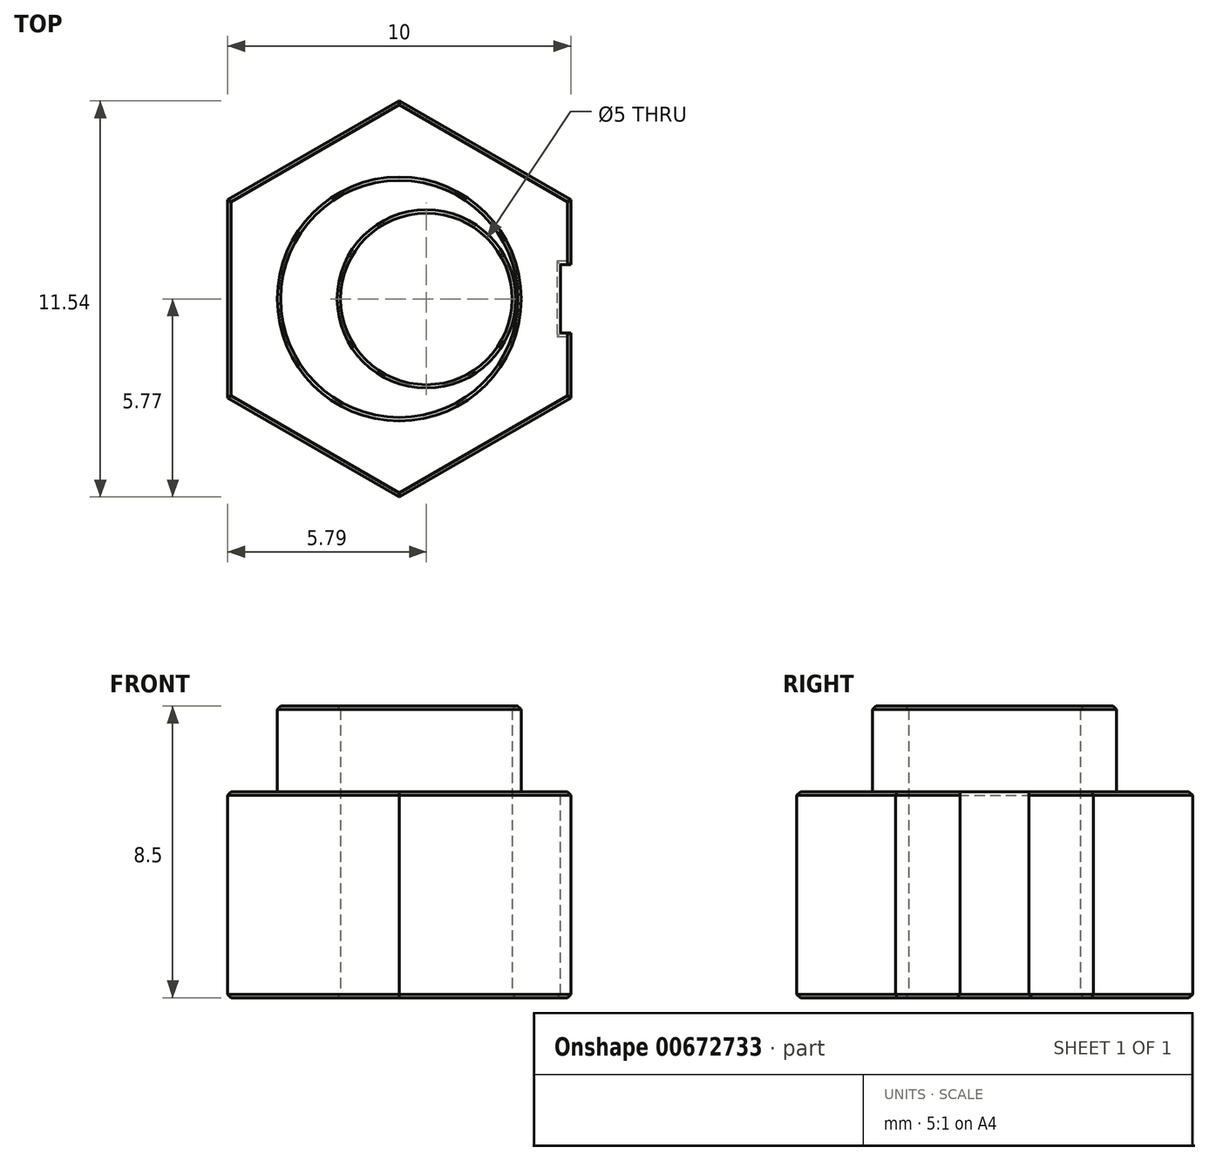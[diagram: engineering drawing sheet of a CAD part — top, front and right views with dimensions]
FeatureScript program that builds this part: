
annotation { "Feature Type Name" : "Feature", "Feature Type Description" : "" }
export const myFeature = defineFeature(function(context is Context, id is Id, definition is map)
    precondition{}
    {
        {
            var Q0;
            Q0=qCreatedBy(makeId("Top.planeOp"),FACE);
            var sketch = newSketch(context, id + "F0", { "sketchPlane" : qUnion([Q0])});
            skCircle(sketch, "E0.cCircle", {"center": v(0, 0) * mm, "radius": 5 * mm, "construction": true});
            skLineSegment(sketch, "E0.0", {"start": v(5, 2.89) * mm, "end": v(5, -2.89) * mm});
            skLineSegment(sketch, "E0.1", {"start": v(5, -2.89) * mm, "end": v(0, -5.77) * mm});
            skLineSegment(sketch, "E0.2", {"start": v(0, -5.77) * mm, "end": v(-5, -2.89) * mm});
            skLineSegment(sketch, "E0.3", {"start": v(-5, -2.89) * mm, "end": v(-5, 2.89) * mm});
            skLineSegment(sketch, "E0.4", {"start": v(-5, 2.89) * mm, "end": v(0, 5.77) * mm});
            skLineSegment(sketch, "E0.5", {"start": v(0, 5.77) * mm, "end": v(5, 2.89) * mm});
            skPoint(sketch, "E0.0.midPoint", {"position": v(5, 0) * mm});
            skSolve(sketch);
        }
        {
            var Q0;
            Q0=makeQuery(id+"F0.imprint","IMPRINT",FACE,{"disambiguationData":[TD([[makeQuery(id+"F0.imprint","IMPRINT",EDGE,{"derivedFrom":sQuery(id+"F0.wireOp",EDGE,"E0.0")}),-1.0]])]});
            extrude(context, id + "F1", {"entities" : qUnion([Q0]), "depth" : 6 * mm, "offsetDistance" : 25 * mm});
        }
        {
            var Q0;
            Q0=makeQuery(id+"F1.opExtrude","CAP_FACE",FACE,{"disambiguationData":[OSD([sQuery(id+"F0.wireOp",EDGE,"E0.0"),sQuery(id+"F0.wireOp",EDGE,"E0.1"),sQuery(id+"F0.wireOp",EDGE,"E0.2"),sQuery(id+"F0.wireOp",EDGE,"E0.3"),sQuery(id+"F0.wireOp",EDGE,"E0.4"),sQuery(id+"F0.wireOp",EDGE,"E0.5")])],"isStart":false});
            var sketch = newSketch(context, id + "F2", { "sketchPlane" : qUnion([Q0])});
            skCircle(sketch, "E1", {"center": v(0, 0) * mm, "radius": 3.56 * mm});
            skCircle(sketch, "E2", {"center": v(0.79, 0) * mm, "radius": 2.5 * mm});
            skSolve(sketch);
        }
        {
            var Q0;
            Q0=makeQuery(id+"F2.imprint","IMPRINT",FACE,{"disambiguationData":[TD([[makeQuery(id+"F2.imprint","IMPRINT",EDGE,{"derivedFrom":sQuery(id+"F2.wireOp",EDGE,"E1")}),1.0]])]});
            extrude(context, id + "F3", {"entities" : qUnion([Q0]), "operationType" : NewBodyOperationType.ADD, "depth" : 2.5 * mm, "offsetDistance" : 25 * mm});
        }
        {
            var Q0;
            {var subQ0=sQuery(id+"F0.wireOp",EDGE,"E0.2");var subQ1=sQuery(id+"F0.wireOp",EDGE,"E0.1");var subQ2=sQuery(id+"F0.wireOp",EDGE,"E0.3");var subQ3=sQuery(id+"F0.wireOp",EDGE,"E0.0");var subQ4=sQuery(id+"F0.wireOp",EDGE,"E0.4");var subQ5=sQuery(id+"F0.wireOp",EDGE,"E0.5");Q0=makeQuery(id+"F3.boolean.opBoolean","SPLIT",FACE,{"disambiguationData":[TD([makeQuery(id+"F1.opExtrude","SWEPT_FACE",FACE,{"disambiguationData":[OSD([subQ3])]})])],"derivedFrom":makeQuery(id+"F1.opExtrude","CAP_FACE",FACE,{"disambiguationData":[OSD([subQ3,subQ1,subQ0,subQ2,subQ4,subQ5])],"isStart":false})});}
            var sketch = newSketch(context, id + "F4", { "sketchPlane" : qUnion([Q0])});
            skLineSegment(sketch, "E3.bottom", {"start": v(5, 1) * mm, "end": v(4.7, 1) * mm});
            skLineSegment(sketch, "E3.top", {"start": v(5, -1) * mm, "end": v(4.7, -1) * mm});
            skLineSegment(sketch, "E3.left", {"start": v(5, 1) * mm, "end": v(5, -1) * mm});
            skLineSegment(sketch, "E3.right", {"start": v(4.7, 1) * mm, "end": v(4.7, -1) * mm});
            skLineSegment(sketch, "E4", {"start": v(0, 0) * mm, "end": v(5, 0) * mm, "construction": true});
            skSolve(sketch);
        }
        {
            var Q0;
            Q0=makeQuery(id+"F4.imprint","IMPRINT",FACE,{"disambiguationData":[TD([[makeQuery(id+"F4.imprint","IMPRINT",EDGE,{"derivedFrom":sQuery(id+"F4.wireOp",EDGE,"E3.bottom")}),1.0]])]});
            extrude(context, id + "F5", {"entities" : qUnion([Q0]), "operationType" : NewBodyOperationType.REMOVE, "oppositeDirection" : true, "depth" : 25 * mm, "offsetDistance" : 25 * mm});
        }
        {
            var Q0;
            Q0=makeQuery(id+"F3.boolean.opBoolean","SPLIT",FACE,{"disambiguationData":[TD([makeQuery(id+"F3.opExtrude","SWEPT_FACE",FACE,{"disambiguationData":[OSD([sQuery(id+"F2.wireOp",EDGE,"E2")])]})])],"derivedFrom":makeQuery(id+"F1.opExtrude","CAP_FACE",FACE,{"disambiguationData":[OSD([sQuery(id+"F0.wireOp",EDGE,"E0.0"),sQuery(id+"F0.wireOp",EDGE,"E0.1"),sQuery(id+"F0.wireOp",EDGE,"E0.2"),sQuery(id+"F0.wireOp",EDGE,"E0.3"),sQuery(id+"F0.wireOp",EDGE,"E0.4"),sQuery(id+"F0.wireOp",EDGE,"E0.5")])],"isStart":false})});
            var sketch = newSketch(context, id + "F6", { "sketchPlane" : qUnion([Q0])});
            skSolve(sketch);
        }
        {
            var Q0;
            Q0=makeQuery(id+"F6.imprint","IMPRINT",FACE,{"disambiguationData":[TD([[makeQuery(id+"F6.imprint","IMPRINT",EDGE,{"derivedFrom":makeQuery(id+"F3.opExtrude","CAP_EDGE",EDGE,{"disambiguationData":[OSD([sQuery(id+"F2.wireOp",EDGE,"E2")])],"isStart":true})}),1.0]])]});
            extrude(context, id + "F7", {"entities" : qUnion([Q0]), "operationType" : NewBodyOperationType.REMOVE, "oppositeDirection" : true, "depth" : 25 * mm, "offsetDistance" : 25 * mm});
        }
        {
            var Q0;
            Q0=makeQuery(id+"F1.opExtrude","CAP_EDGE",EDGE,{"disambiguationData":[OSD([sQuery(id+"F0.wireOp",EDGE,"E0.2")])],"isStart":false});
            var Q1;
            Q1=makeQuery(id+"F1.opExtrude","CAP_EDGE",EDGE,{"disambiguationData":[OSD([sQuery(id+"F0.wireOp",EDGE,"E0.1")])],"isStart":false});
            var Q2;
            {var subQ0=sQuery(id+"F0.wireOp",EDGE,"E0.0");var subQ1=sQuery(id+"F0.wireOp",EDGE,"E0.1");Q2=makeQuery(id+"F5.boolean.opBoolean","SPLIT",EDGE,{"disambiguationData":[TD([makeQuery(id+"F1.opExtrude","SWEPT_FACE",FACE,{"disambiguationData":[OSD([subQ1])]})])],"derivedFrom":makeQuery(id+"F1.opExtrude","CAP_EDGE",EDGE,{"disambiguationData":[OSD([subQ0])],"isStart":false})});}
            var Q3;
            Q3=makeQuery(id+"F5.boolean.opBoolean","COPY",EDGE,{"derivedFrom":makeQuery(id+"F5.opExtrude","CAP_EDGE",EDGE,{"disambiguationData":[OSD([sQuery(id+"F4.wireOp",EDGE,"E3.right")])],"isStart":true})});
            var Q4;
            Q4=makeQuery(id+"F5.boolean.opBoolean","COPY",EDGE,{"derivedFrom":makeQuery(id+"F5.opExtrude","CAP_EDGE",EDGE,{"disambiguationData":[OSD([sQuery(id+"F4.wireOp",EDGE,"E3.top")])],"isStart":true})});
            var Q5;
            Q5=makeQuery(id+"F5.boolean.opBoolean","COPY",EDGE,{"derivedFrom":makeQuery(id+"F5.opExtrude","CAP_EDGE",EDGE,{"disambiguationData":[OSD([sQuery(id+"F4.wireOp",EDGE,"E3.bottom")])],"isStart":true})});
            var Q6;
            {var subQ0=sQuery(id+"F0.wireOp",EDGE,"E0.0");var subQ1=sQuery(id+"F0.wireOp",EDGE,"E0.5");Q6=makeQuery(id+"F5.boolean.opBoolean","SPLIT",EDGE,{"disambiguationData":[TD([makeQuery(id+"F1.opExtrude","SWEPT_FACE",FACE,{"disambiguationData":[OSD([subQ1])]})])],"derivedFrom":makeQuery(id+"F1.opExtrude","CAP_EDGE",EDGE,{"disambiguationData":[OSD([subQ0])],"isStart":false})});}
            var Q7;
            Q7=makeQuery(id+"F1.opExtrude","CAP_EDGE",EDGE,{"disambiguationData":[OSD([sQuery(id+"F0.wireOp",EDGE,"E0.5")])],"isStart":false});
            var Q8;
            Q8=makeQuery(id+"F1.opExtrude","CAP_EDGE",EDGE,{"disambiguationData":[OSD([sQuery(id+"F0.wireOp",EDGE,"E0.4")])],"isStart":false});
            var Q9;
            Q9=makeQuery(id+"F1.opExtrude","CAP_EDGE",EDGE,{"disambiguationData":[OSD([sQuery(id+"F0.wireOp",EDGE,"E0.3")])],"isStart":false});
            var Q10;
            Q10=makeQuery(id+"F3.opExtrude","CAP_EDGE",EDGE,{"disambiguationData":[OSD([sQuery(id+"F2.wireOp",EDGE,"E1")])],"isStart":false});
            var Q11;
            Q11=makeQuery(id+"F3.opExtrude","CAP_EDGE",EDGE,{"disambiguationData":[OSD([sQuery(id+"F2.wireOp",EDGE,"E2")])],"isStart":false});
            var Q12;
            Q12=makeQuery(id+"F7.boolean.opBoolean","INTERSECT",EDGE,{"derivedFrom":[makeQuery(id+"F1.opExtrude","CAP_FACE",FACE,{"disambiguationData":[OSD([sQuery(id+"F0.wireOp",EDGE,"E0.0"),sQuery(id+"F0.wireOp",EDGE,"E0.1"),sQuery(id+"F0.wireOp",EDGE,"E0.2"),sQuery(id+"F0.wireOp",EDGE,"E0.3"),sQuery(id+"F0.wireOp",EDGE,"E0.4"),sQuery(id+"F0.wireOp",EDGE,"E0.5")])],"isStart":true}),makeQuery(id+"F7.opExtrude","SWEPT_FACE",FACE,{"disambiguationData":[OSD([sQuery(id+"F2.wireOp",EDGE,"E2")])]})]});
            var Q13;
            Q13=makeQuery(id+"F1.opExtrude","CAP_EDGE",EDGE,{"disambiguationData":[OSD([sQuery(id+"F0.wireOp",EDGE,"E0.1")])],"isStart":true});
            var Q14;
            Q14=makeQuery(id+"F1.opExtrude","CAP_EDGE",EDGE,{"disambiguationData":[OSD([sQuery(id+"F0.wireOp",EDGE,"E0.2")])],"isStart":true});
            var Q15;
            Q15=makeQuery(id+"F1.opExtrude","CAP_EDGE",EDGE,{"disambiguationData":[OSD([sQuery(id+"F0.wireOp",EDGE,"E0.3")])],"isStart":true});
            var Q16;
            Q16=makeQuery(id+"F1.opExtrude","CAP_EDGE",EDGE,{"disambiguationData":[OSD([sQuery(id+"F0.wireOp",EDGE,"E0.4")])],"isStart":true});
            var Q17;
            Q17=makeQuery(id+"F1.opExtrude","CAP_EDGE",EDGE,{"disambiguationData":[OSD([sQuery(id+"F0.wireOp",EDGE,"E0.5")])],"isStart":true});
            var Q18;
            {var subQ0=sQuery(id+"F0.wireOp",EDGE,"E0.0");var subQ1=sQuery(id+"F0.wireOp",EDGE,"E0.1");Q18=makeQuery(id+"F5.boolean.opBoolean","SPLIT",EDGE,{"disambiguationData":[TD([makeQuery(id+"F1.opExtrude","SWEPT_FACE",FACE,{"disambiguationData":[OSD([subQ1])]})])],"derivedFrom":makeQuery(id+"F1.opExtrude","CAP_EDGE",EDGE,{"disambiguationData":[OSD([subQ0])],"isStart":true})});}
            var Q19;
            {var subQ0=sQuery(id+"F0.wireOp",EDGE,"E0.0");var subQ1=sQuery(id+"F0.wireOp",EDGE,"E0.5");Q19=makeQuery(id+"F5.boolean.opBoolean","SPLIT",EDGE,{"disambiguationData":[TD([makeQuery(id+"F1.opExtrude","SWEPT_FACE",FACE,{"disambiguationData":[OSD([subQ1])]})])],"derivedFrom":makeQuery(id+"F1.opExtrude","CAP_EDGE",EDGE,{"disambiguationData":[OSD([subQ0])],"isStart":true})});}
            var Q20;
            Q20=makeQuery(id+"F5.boolean.opBoolean","INTERSECT",EDGE,{"derivedFrom":[makeQuery(id+"F1.opExtrude","CAP_FACE",FACE,{"disambiguationData":[OSD([sQuery(id+"F0.wireOp",EDGE,"E0.0"),sQuery(id+"F0.wireOp",EDGE,"E0.1"),sQuery(id+"F0.wireOp",EDGE,"E0.2"),sQuery(id+"F0.wireOp",EDGE,"E0.3"),sQuery(id+"F0.wireOp",EDGE,"E0.4"),sQuery(id+"F0.wireOp",EDGE,"E0.5")])],"isStart":true}),makeQuery(id+"F5.opExtrude","SWEPT_FACE",FACE,{"disambiguationData":[OSD([sQuery(id+"F4.wireOp",EDGE,"E3.bottom")])]})]});
            var Q21;
            Q21=makeQuery(id+"F5.boolean.opBoolean","INTERSECT",EDGE,{"derivedFrom":[makeQuery(id+"F1.opExtrude","CAP_FACE",FACE,{"disambiguationData":[OSD([sQuery(id+"F0.wireOp",EDGE,"E0.0"),sQuery(id+"F0.wireOp",EDGE,"E0.1"),sQuery(id+"F0.wireOp",EDGE,"E0.2"),sQuery(id+"F0.wireOp",EDGE,"E0.3"),sQuery(id+"F0.wireOp",EDGE,"E0.4"),sQuery(id+"F0.wireOp",EDGE,"E0.5")])],"isStart":true}),makeQuery(id+"F5.opExtrude","SWEPT_FACE",FACE,{"disambiguationData":[OSD([sQuery(id+"F4.wireOp",EDGE,"E3.right")])]})]});
            var Q22;
            Q22=makeQuery(id+"F5.boolean.opBoolean","INTERSECT",EDGE,{"derivedFrom":[makeQuery(id+"F1.opExtrude","CAP_FACE",FACE,{"disambiguationData":[OSD([sQuery(id+"F0.wireOp",EDGE,"E0.0"),sQuery(id+"F0.wireOp",EDGE,"E0.1"),sQuery(id+"F0.wireOp",EDGE,"E0.2"),sQuery(id+"F0.wireOp",EDGE,"E0.3"),sQuery(id+"F0.wireOp",EDGE,"E0.4"),sQuery(id+"F0.wireOp",EDGE,"E0.5")])],"isStart":true}),makeQuery(id+"F5.opExtrude","SWEPT_FACE",FACE,{"disambiguationData":[OSD([sQuery(id+"F4.wireOp",EDGE,"E3.top")])]})]});
            chamfer(context, id + "F8", {"entities" : qUnion([Q0, Q1, Q2, Q3, Q4, Q5, Q6, Q7, Q8, Q9, Q10, Q11, Q12, Q13, Q14, Q15, Q16, Q17, Q18, Q19, Q20, Q21, Q22]), "width" : .1 * mm, "tangentPropagation" : true});
        }
    });
